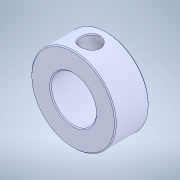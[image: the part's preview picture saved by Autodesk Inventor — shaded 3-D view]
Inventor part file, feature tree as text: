
AUTODESK INVENTOR PART (.ipt)
format: ipt  version: 2020.2 (Build 242310000, 310)  size: 190,464 bytes
history: native  units: in
note: dims shown in document units (in); Inventor stores cm internally (conversion verified against a paired STEP export)
features: chamfer x1
ambient origin geometry x8: Origin, YZ Plane, XZ Plane, XY Plane, X Axis, Y Axis, Z Axis, Center Point
bodies: Solid1 (feature_tree)
feature tree (1):
  chamfer  "Chamfer1"  [1 undecoded]
note: 1 required parameter value undecoded (feature->parameter linkage not recoverable at this tier; creation-order binding heuristic only, values carry confidence <= 0.55)
